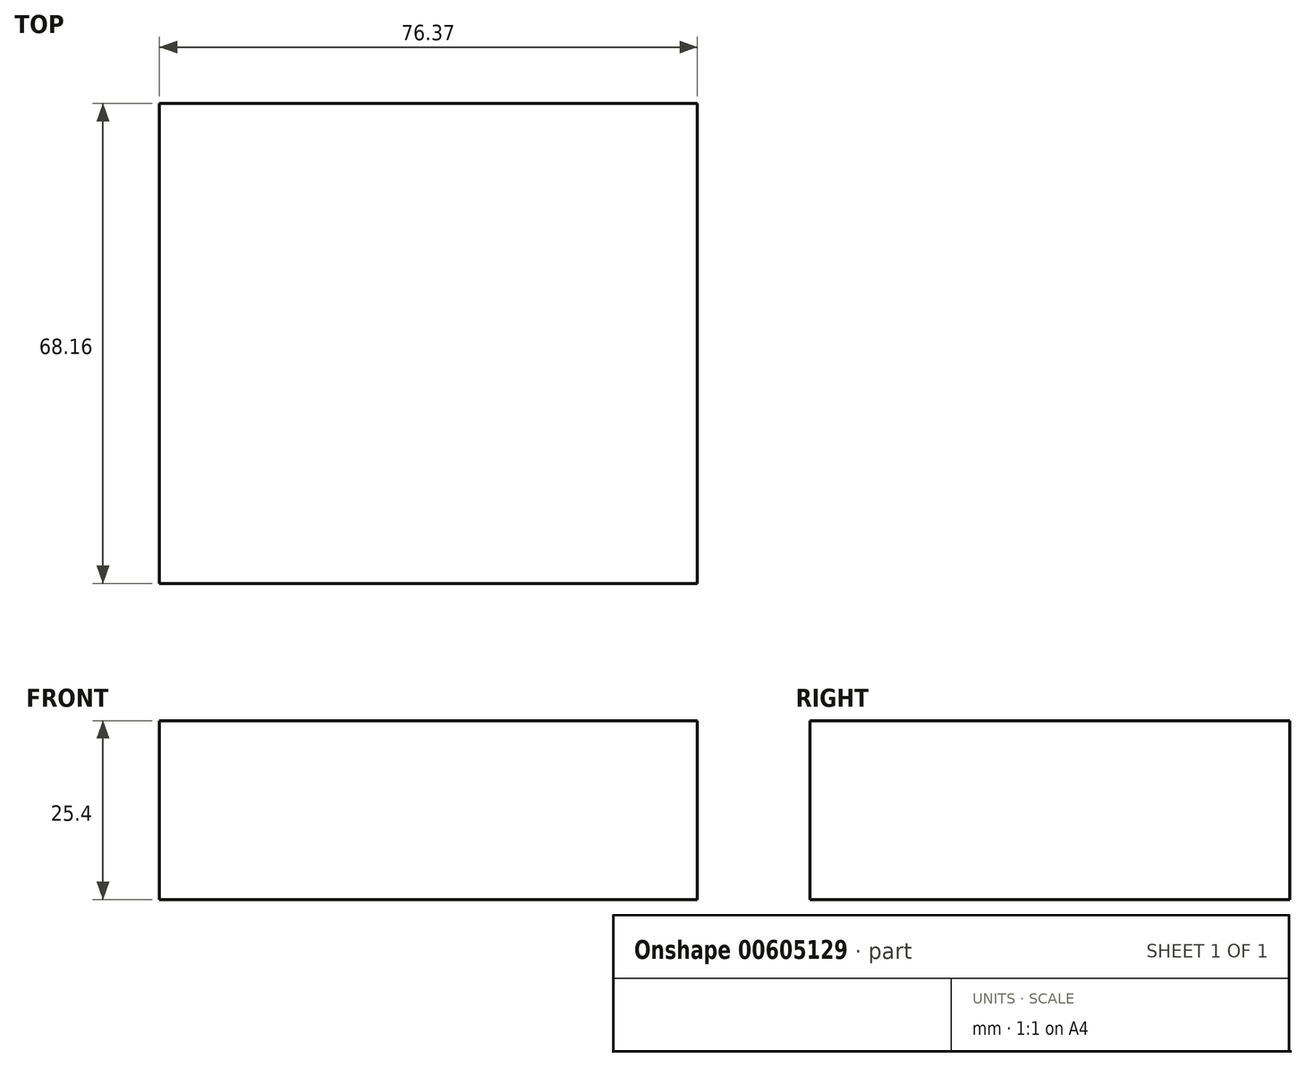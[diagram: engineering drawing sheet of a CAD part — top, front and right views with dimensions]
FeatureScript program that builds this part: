
annotation { "Feature Type Name" : "Feature", "Feature Type Description" : "" }
export const myFeature = defineFeature(function(context is Context, id is Id, definition is map)
    precondition{}
    {
        {
            var Q0;
            Q0=qCreatedBy(makeId("Top.planeOp"),FACE);
            var sketch = newSketch(context, id + "F0", { "sketchPlane" : qUnion([Q0])});
            skLineSegment(sketch, "E0.bottom", {"start": v(-45.6, 22.75) * mm, "end": v(30.77, 22.75) * mm});
            skLineSegment(sketch, "E0.top", {"start": v(-45.6, -45.41) * mm, "end": v(30.77, -45.41) * mm});
            skLineSegment(sketch, "E0.left", {"start": v(-45.6, 22.75) * mm, "end": v(-45.6, -45.41) * mm});
            skLineSegment(sketch, "E0.right", {"start": v(30.77, 22.75) * mm, "end": v(30.77, -45.41) * mm});
            skSolve(sketch);
        }
        {
            var Q0;
            Q0 = qSketchRegion(id + "F0", true);
            extrude(context, id + "F1", {"entities" : qUnion([Q0]), "depth" : 25.4 * mm, "offsetDistance" : 25.4 * mm});
        }
    });
